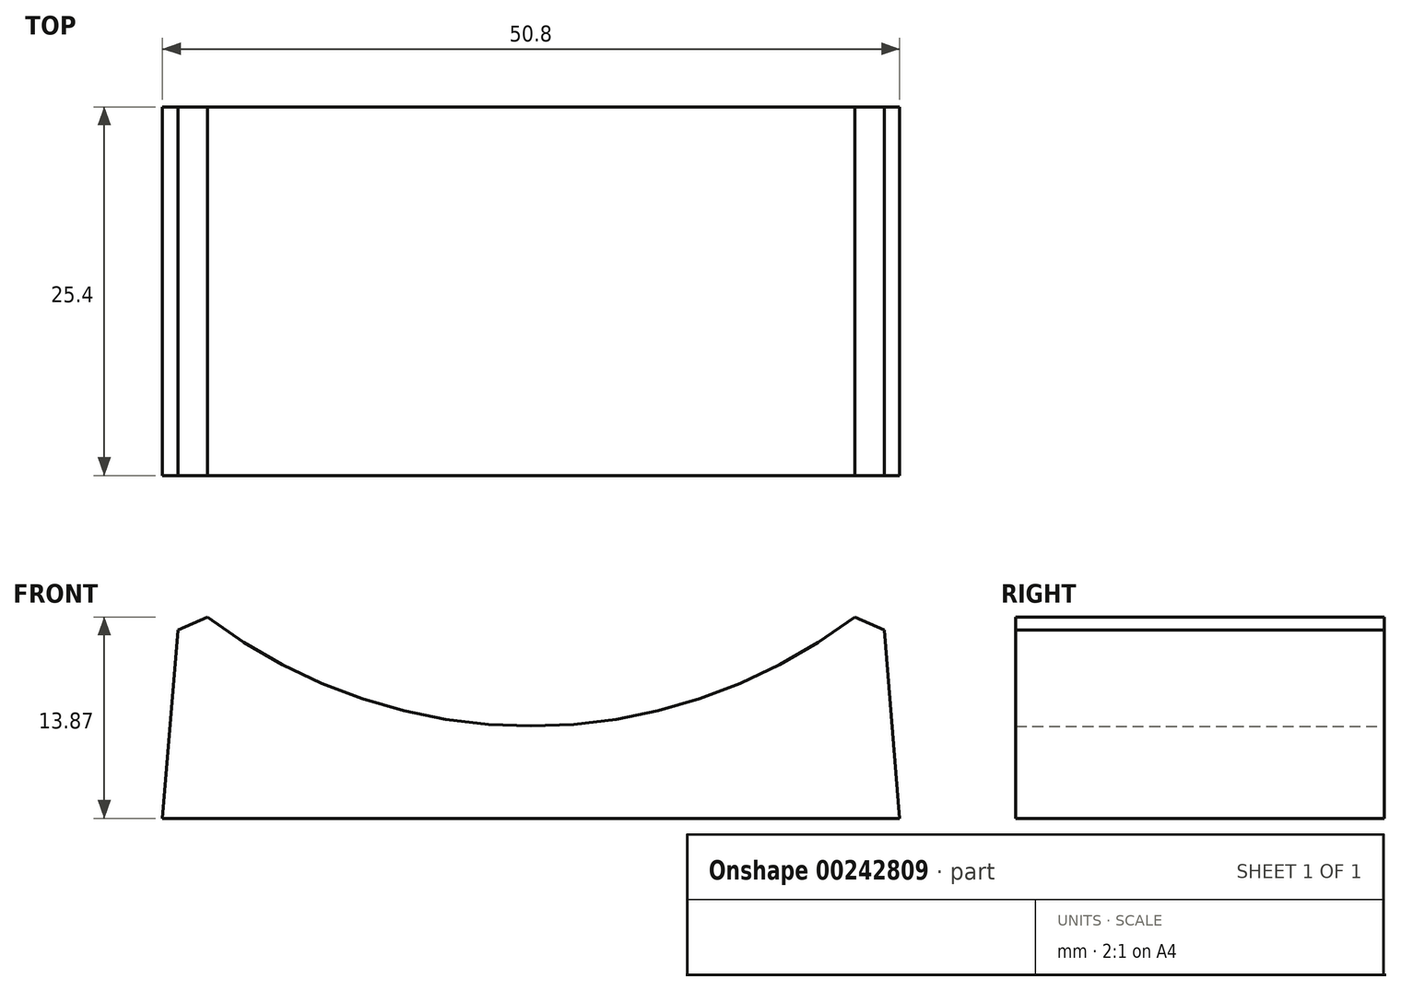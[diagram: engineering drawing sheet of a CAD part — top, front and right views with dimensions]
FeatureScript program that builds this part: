
annotation { "Feature Type Name" : "Feature", "Feature Type Description" : "" }
export const myFeature = defineFeature(function(context is Context, id is Id, definition is map)
    precondition{}
    {
        {
            var Q0;
            Q0=qCreatedBy(makeId("Front.planeOp"),FACE);
            var sketch = newSketch(context, id + "F0", { "sketchPlane" : qUnion([Q0])});
            skLineSegment(sketch, "E0", {"start": v(0, 0) * mm, "end": v(50.8, 0) * mm});
            skArc(sketch, "E1", {"start": v(1.26, 15.36) * mm, "mid": v(25.4, 6.35) * mm, "end": v(49.54, 15.36) * mm});
            skLineSegment(sketch, "E2", {"start": v(0, 0) * mm, "end": v(1.26, 15.36) * mm});
            skLineSegment(sketch, "E3.MirrorCS", {"start": v(50.8, 0) * mm, "end": v(49.54, 15.36) * mm});
            skPoint(sketch, "E4.start.orphan", {"position": v(25.4, 0) * mm});
            skSolve(sketch);
        }
        {
            var Q0;
            Q0 = qSketchRegion(id + "F0", true);
            extrude(context, id + "F1", {"entities" : qUnion([Q0]), "depth" : 25.4 * mm});
        }
        {
            var Q0;
            Q0=makeQuery(id+"F1.opExtrude","SWEPT_EDGE",EDGE,{"disambiguationData":[OSD([sQuery(id+"F0.wireOp",EDGE,"E1"),sQuery(id+"F0.wireOp",EDGE,"E2")])]});
            var Q1;
            Q1=makeQuery(id+"F1.opExtrude","SWEPT_EDGE",EDGE,{"disambiguationData":[OSD([sQuery(id+"F0.wireOp",EDGE,"E1"),sQuery(id+"F0.wireOp",EDGE,"E3.MirrorCS")])]});
            chamfer(context, id + "F2", {"entities" : qUnion([Q0, Q1]), "width" : 1.27 * mm, "tangentPropagation" : true});
        }
    });
